# Revit family: HL_Трап для внутренних помещений_HL80.2
name_source: partatom
category: Instalační zařizovací předměty
revit_build: Autodesk Revit 2016 (Build: 20151007_0715(x64)
units: mm (PartAtom-declared; Revit-internal decimal feet)

## family parameters
Bod výpočtu místnosti = Ano
Kóta kulaté spojky = Použít průměr
Nadpis OmniClass = Deck Waste Water Drains
Ořezat dutým tvarem při načtení = Ne
Sdílené = Ano
Typ součásti = Normální
Vždy vertikální = Ano
Založené na pracovní rovině = Ne
Číslo OmniClass = 23.70.50.21.24.14

## types (1)
- HL80.2
    EAN = 9003076700820
    Klíčová poznámka = HL80.2
    Komentáře k typům = HL80.2 Трап для внутренних помещений DN50/75 с запахозапирающим устройством, вентильной плитой и стояком 100мм
    Model = HL80.2
    Popis = Трапы для внутренних помещений
    Připojení CW = Ne
    Připojení HW = Ne
    Připojení odpadu = Ano
    Připojení ventilace = Ne
    URL = http://www.hutterer-lechner.com
    Výrobce = HL Hutterer & Lechner GmbH
    ВЕС = 0,54 [kg]
    ВЫСОТА МОНТАЖА = 102mm
    МАТЕРИАЛ = PP/PE
    НАСАДКА = 12-75mm / 100x100mm / PP
    ПРОИЗВОДИТЕЛЬНОСТЬ = 0,5 l/sec
    ПРОПУСКНАЯ СПОСОБНОСТЬ = 0.5 L/s
    РАЗМЕР = DN50/75
    РЕШЁТКА = 94x94 mm mit Standrohr / Kunststoff

## geometry (parser evidence)
native form markers: Sweep x33
no freeform markers — native parametric forms only
